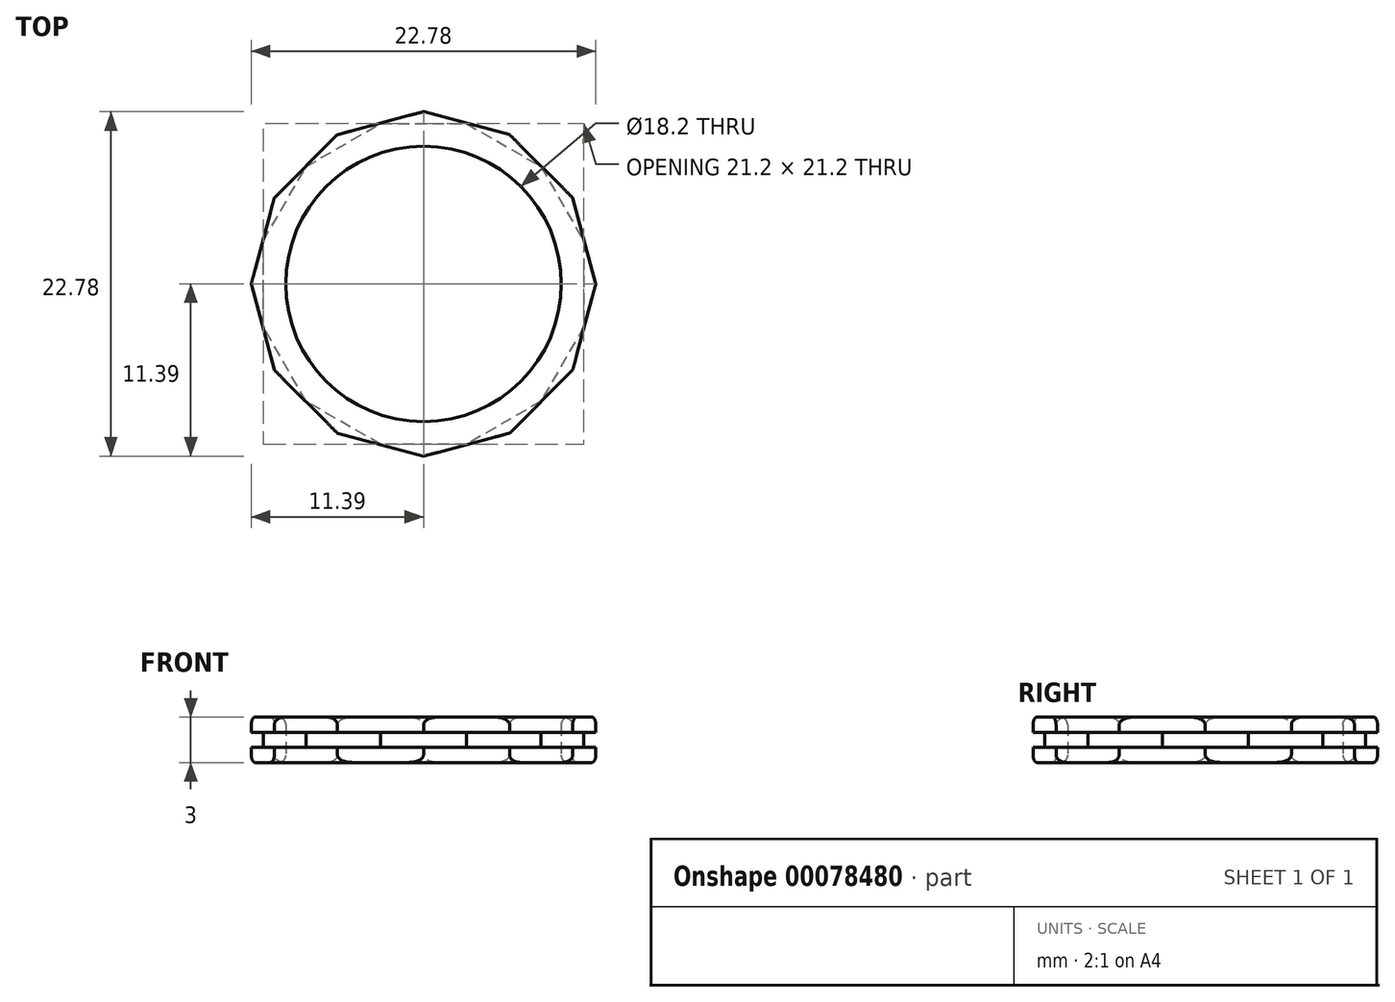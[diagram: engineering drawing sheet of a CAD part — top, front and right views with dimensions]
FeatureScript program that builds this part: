
annotation { "Feature Type Name" : "Feature", "Feature Type Description" : "" }
export const myFeature = defineFeature(function(context is Context, id is Id, definition is map)
    precondition{}
    {
        {
            var Q0;
            Q0=qCreatedBy(makeId("Top.planeOp"),FACE);
            var sketch = newSketch(context, id + "F0", { "sketchPlane" : qUnion([Q0])});
            skCircle(sketch, "E0", {"center": v(0, 0) * mm, "radius": 9.1 * mm});
            skSolve(sketch);
        }
        {
            var Q0;
            Q0=qCreatedBy(makeId("Top.planeOp"),FACE);
            var sketch = newSketch(context, id + "F1", { "sketchPlane" : qUnion([Q0])});
            skCircle(sketch, "E1.cCircle", {"center": v(0, 0) * mm, "radius": 10.6 * mm, "construction": true});
            skLineSegment(sketch, "E1.0", {"start": v(-7.76, -7.76) * mm, "end": v(-10.6, -2.84) * mm});
            skLineSegment(sketch, "E1.1", {"start": v(-10.6, -2.84) * mm, "end": v(-10.6, 2.84) * mm});
            skLineSegment(sketch, "E1.2", {"start": v(-10.6, 2.84) * mm, "end": v(-7.76, 7.76) * mm});
            skLineSegment(sketch, "E1.3", {"start": v(-7.76, 7.76) * mm, "end": v(-2.84, 10.6) * mm});
            skLineSegment(sketch, "E1.4", {"start": v(-2.84, 10.6) * mm, "end": v(2.84, 10.6) * mm});
            skLineSegment(sketch, "E1.5", {"start": v(2.84, 10.6) * mm, "end": v(7.76, 7.76) * mm});
            skLineSegment(sketch, "E1.6", {"start": v(7.76, 7.76) * mm, "end": v(10.6, 2.84) * mm});
            skLineSegment(sketch, "E1.7", {"start": v(10.6, 2.84) * mm, "end": v(10.6, -2.84) * mm});
            skLineSegment(sketch, "E1.8", {"start": v(10.6, -2.84) * mm, "end": v(7.76, -7.76) * mm});
            skLineSegment(sketch, "E1.9", {"start": v(7.76, -7.76) * mm, "end": v(2.84, -10.6) * mm});
            skLineSegment(sketch, "E1.10", {"start": v(2.84, -10.6) * mm, "end": v(-2.84, -10.6) * mm});
            skLineSegment(sketch, "E1.11", {"start": v(-2.84, -10.6) * mm, "end": v(-7.76, -7.76) * mm});
            skPoint(sketch, "E1.0.midPoint", {"position": v(-9.18, -5.3) * mm});
            skLineSegment(sketch, "E2", {"start": v(0, 0) * mm, "end": v(-10.6, 0) * mm, "construction": true});
            skSolve(sketch);
        }
        {
            var Q0;
            Q0=qSketchRegion(id+"F1",true);
            extrude(context, id + "F2", {"entities" : qUnion([Q0]), "endBound" : BoundingType.SYMMETRIC, "depth" : 1 * mm});
        }
        {
            var Q0;
            Q0=makeQuery(id+"F2.opExtrude","CAP_FACE",FACE,{"disambiguationData":[OSD([sQuery(id+"F1.wireOp",EDGE,"E1.0"),sQuery(id+"F1.wireOp",EDGE,"E1.1"),sQuery(id+"F1.wireOp",EDGE,"E1.2"),sQuery(id+"F1.wireOp",EDGE,"E1.3"),sQuery(id+"F1.wireOp",EDGE,"E1.4"),sQuery(id+"F1.wireOp",EDGE,"E1.5"),sQuery(id+"F1.wireOp",EDGE,"E1.6"),sQuery(id+"F1.wireOp",EDGE,"E1.7"),sQuery(id+"F1.wireOp",EDGE,"E1.8"),sQuery(id+"F1.wireOp",EDGE,"E1.9"),sQuery(id+"F1.wireOp",EDGE,"E1.10"),sQuery(id+"F1.wireOp",EDGE,"E1.11")])],"isStart":false});
            var sketch = newSketch(context, id + "F3", { "sketchPlane" : qUnion([Q0])});
            skCircle(sketch, "E3.cCircle", {"center": v(0, 0) * mm, "radius": 11 * mm, "construction": true});
            skLineSegment(sketch, "E3.0", {"start": v(-11.39, 0) * mm, "end": v(-9.86, 5.7) * mm});
            skLineSegment(sketch, "E3.1", {"start": v(-9.86, 5.7) * mm, "end": v(-5.7, 9.86) * mm});
            skLineSegment(sketch, "E3.2", {"start": v(-5.7, 9.86) * mm, "end": v(0, 11.39) * mm});
            skLineSegment(sketch, "E3.3", {"start": v(0, 11.39) * mm, "end": v(5.7, 9.86) * mm});
            skLineSegment(sketch, "E3.4", {"start": v(5.7, 9.86) * mm, "end": v(9.86, 5.7) * mm});
            skLineSegment(sketch, "E3.5", {"start": v(9.86, 5.7) * mm, "end": v(11.39, 0) * mm});
            skLineSegment(sketch, "E3.6", {"start": v(11.39, 0) * mm, "end": v(9.86, -5.7) * mm});
            skLineSegment(sketch, "E3.7", {"start": v(9.86, -5.7) * mm, "end": v(5.7, -9.86) * mm});
            skLineSegment(sketch, "E3.8", {"start": v(5.7, -9.86) * mm, "end": v(0, -11.39) * mm});
            skLineSegment(sketch, "E3.9", {"start": v(0, -11.39) * mm, "end": v(-5.7, -9.86) * mm});
            skLineSegment(sketch, "E3.10", {"start": v(-5.7, -9.86) * mm, "end": v(-9.86, -5.7) * mm});
            skLineSegment(sketch, "E3.11", {"start": v(-9.86, -5.7) * mm, "end": v(-11.39, 0) * mm});
            skPoint(sketch, "E3.0.midPoint", {"position": v(-10.63, 2.85) * mm});
            skLineSegment(sketch, "E4", {"start": v(0, 0) * mm, "end": v(-10.63, 2.85) * mm, "construction": true});
            skSolve(sketch);
        }
        {
            var Q0;
            Q0=qSketchRegion(id+"F3",true);
            extrude(context, id + "F4", {"entities" : qUnion([Q0]), "depth" : 1 * mm});
        }
        {
            var Q0;
            Q0=makeQuery(id+"F4.opExtrude","SWEPT_BODY",BODY,{"disambiguationData":[OSD([sQuery(id+"F3.wireOp",EDGE,"E3.0"),sQuery(id+"F3.wireOp",EDGE,"E3.1"),sQuery(id+"F3.wireOp",EDGE,"E3.2"),sQuery(id+"F3.wireOp",EDGE,"E3.3"),sQuery(id+"F3.wireOp",EDGE,"E3.4"),sQuery(id+"F3.wireOp",EDGE,"E3.5"),sQuery(id+"F3.wireOp",EDGE,"E3.6"),sQuery(id+"F3.wireOp",EDGE,"E3.7"),sQuery(id+"F3.wireOp",EDGE,"E3.8"),sQuery(id+"F3.wireOp",EDGE,"E3.9"),sQuery(id+"F3.wireOp",EDGE,"E3.10"),sQuery(id+"F3.wireOp",EDGE,"E3.11")])]});
            var Q1;
            Q1=qCreatedBy(makeId("Top.planeOp"),FACE);
            mirror(context, id + "F5", {"operationType" : NewBodyOperationType.ADD, "entities" : qUnion([Q0]), "mirrorPlane" : qUnion([Q1])});
        }
        {
            var Q0;
            Q0=qSketchRegion(id+"F0",true);
            extrude(context, id + "F6", {"entities" : qUnion([Q0]), "operationType" : NewBodyOperationType.REMOVE, "endBound" : BoundingType.SYMMETRIC, "depth" : 5 * mm});
        }
        {
            var Q0;
            Q0=makeQuery(id+"F6.boolean.opBoolean","COPY",FACE,{"derivedFrom":makeQuery(id+"F6.opExtrude","SWEPT_FACE",FACE,{"disambiguationData":[OSD([sQuery(id+"F0.wireOp",EDGE,"E0")])]})});
            fillet(context, id + "F7", {"entities" : qUnion([Q0]), "radius" : .5 * mm, "tangentPropagation" : true, "allowEdgeOverflow" : false});
        }
        {
            var Q0;
            Q0=makeQuery(id+"F5.opPattern","COPY",EDGE,{"derivedFrom":makeQuery(id+"F4.opExtrude","CAP_EDGE",EDGE,{"disambiguationData":[OSD([sQuery(id+"F3.wireOp",EDGE,"E3.6")])],"isStart":false}),"instanceName":"1"});
            var Q1;
            Q1=makeQuery(id+"F5.opPattern","COPY",EDGE,{"derivedFrom":makeQuery(id+"F4.opExtrude","CAP_EDGE",EDGE,{"disambiguationData":[OSD([sQuery(id+"F3.wireOp",EDGE,"E3.4")])],"isStart":false}),"instanceName":"1"});
            var Q2;
            Q2=makeQuery(id+"F5.opPattern","COPY",EDGE,{"derivedFrom":makeQuery(id+"F4.opExtrude","CAP_EDGE",EDGE,{"disambiguationData":[OSD([sQuery(id+"F3.wireOp",EDGE,"E3.2")])],"isStart":false}),"instanceName":"1"});
            var Q3;
            Q3=makeQuery(id+"F5.opPattern","COPY",EDGE,{"derivedFrom":makeQuery(id+"F4.opExtrude","CAP_EDGE",EDGE,{"disambiguationData":[OSD([sQuery(id+"F3.wireOp",EDGE,"E3.0")])],"isStart":false}),"instanceName":"1"});
            var Q4;
            Q4=makeQuery(id+"F5.opPattern","COPY",EDGE,{"derivedFrom":makeQuery(id+"F4.opExtrude","CAP_EDGE",EDGE,{"disambiguationData":[OSD([sQuery(id+"F3.wireOp",EDGE,"E3.10")])],"isStart":false}),"instanceName":"1"});
            var Q5;
            Q5=makeQuery(id+"F5.opPattern","COPY",EDGE,{"derivedFrom":makeQuery(id+"F4.opExtrude","CAP_EDGE",EDGE,{"disambiguationData":[OSD([sQuery(id+"F3.wireOp",EDGE,"E3.8")])],"isStart":false}),"instanceName":"1"});
            var Q6;
            Q6=makeQuery(id+"F4.opExtrude","CAP_EDGE",EDGE,{"disambiguationData":[OSD([sQuery(id+"F3.wireOp",EDGE,"E3.9")])],"isStart":false});
            var Q7;
            Q7=makeQuery(id+"F4.opExtrude","CAP_EDGE",EDGE,{"disambiguationData":[OSD([sQuery(id+"F3.wireOp",EDGE,"E3.7")])],"isStart":false});
            var Q8;
            Q8=makeQuery(id+"F4.opExtrude","CAP_EDGE",EDGE,{"disambiguationData":[OSD([sQuery(id+"F3.wireOp",EDGE,"E3.5")])],"isStart":false});
            var Q9;
            Q9=makeQuery(id+"F4.opExtrude","CAP_EDGE",EDGE,{"disambiguationData":[OSD([sQuery(id+"F3.wireOp",EDGE,"E3.3")])],"isStart":false});
            var Q10;
            Q10=makeQuery(id+"F4.opExtrude","CAP_EDGE",EDGE,{"disambiguationData":[OSD([sQuery(id+"F3.wireOp",EDGE,"E3.1")])],"isStart":false});
            var Q11;
            Q11=makeQuery(id+"F4.opExtrude","CAP_EDGE",EDGE,{"disambiguationData":[OSD([sQuery(id+"F3.wireOp",EDGE,"E3.11")])],"isStart":false});
            fillet(context, id + "F8", {"entities" : qUnion([Q0, Q1, Q2, Q3, Q4, Q5, Q6, Q7, Q8, Q9, Q10, Q11]), "radius" : .5 * mm, "tangentPropagation" : true, "allowEdgeOverflow" : false});
        }
    });
